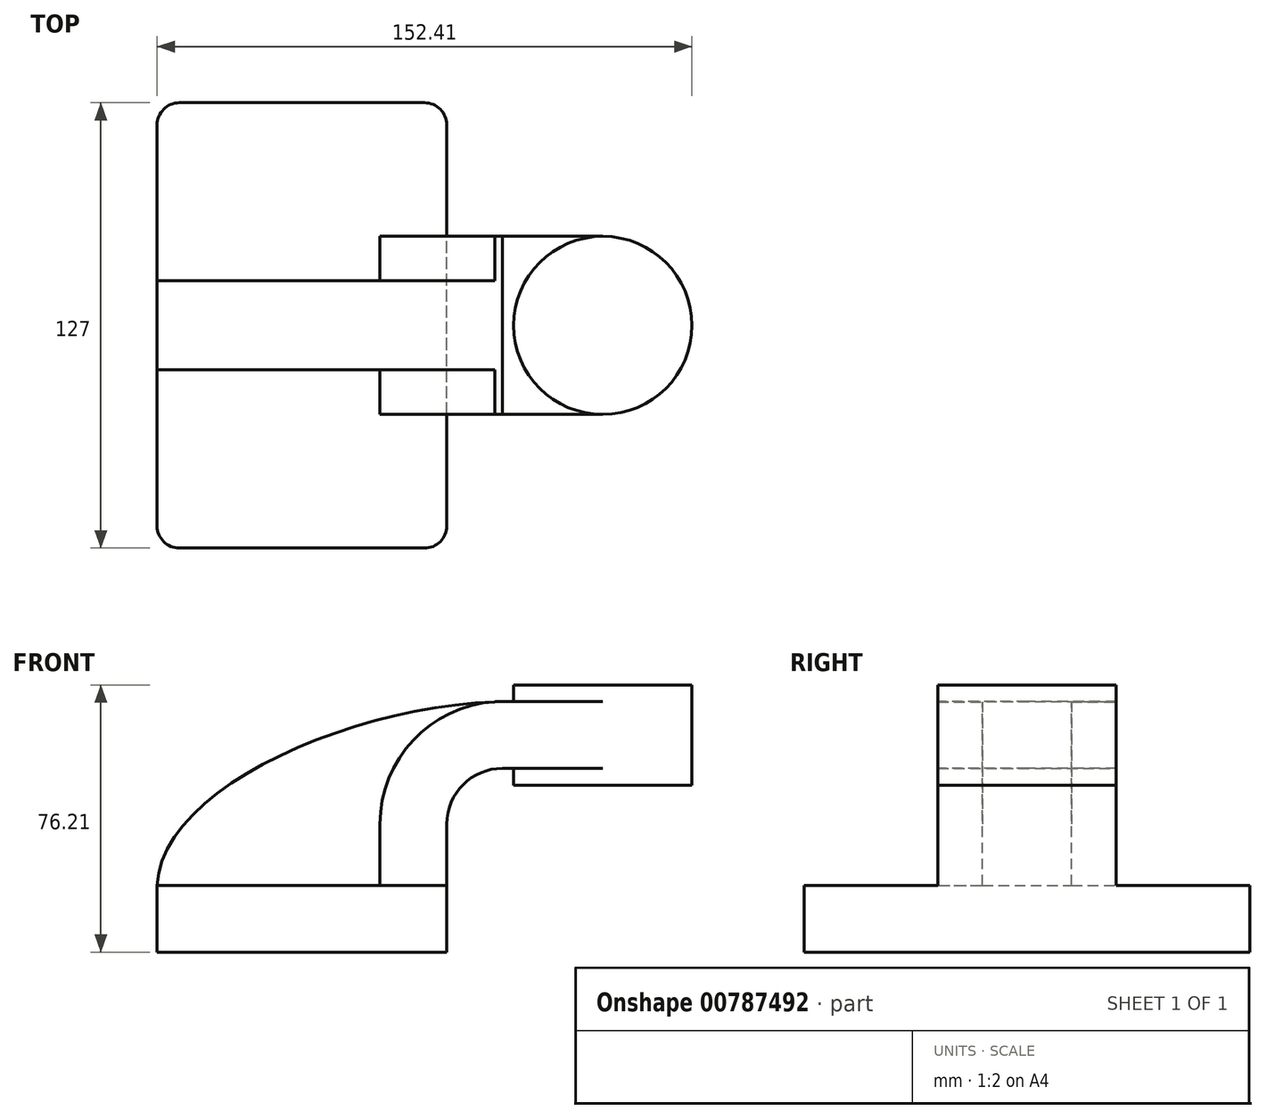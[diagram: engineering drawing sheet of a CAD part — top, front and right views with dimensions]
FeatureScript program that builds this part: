
annotation { "Feature Type Name" : "Feature", "Feature Type Description" : "" }
export const myFeature = defineFeature(function(context is Context, id is Id, definition is map)
    precondition{}
    {
        {
            var Q0;
            Q0=qCreatedBy(makeId("Front.planeOp"),FACE);
            var sketch = newSketch(context, id + "F0", { "sketchPlane" : qUnion([Q0])});
            skLineSegment(sketch, "E0.bottom", {"start": v(41.28, 9.53) * mm, "end": v(-41.27, 9.52) * mm});
            skLineSegment(sketch, "E0.top", {"start": v(41.28, -9.52) * mm, "end": v(-41.27, -9.53) * mm});
            skLineSegment(sketch, "E0.left", {"start": v(41.28, 9.53) * mm, "end": v(41.28, -9.52) * mm});
            skLineSegment(sketch, "E0.right", {"start": v(-41.27, 9.52) * mm, "end": v(-41.27, -9.53) * mm});
            skPoint(sketch, "E0.middle", {"position": v(0, 0) * mm});
            skLineSegment(sketch, "E1", {"start": v(41.27, 9.53) * mm, "end": v(41.27, 27) * mm});
            skArc(sketch, "E2", {"start": v(41.27, 27) * mm, "mid": v(45.92, 38.23) * mm, "end": v(57.15, 42.88) * mm});
            skLineSegment(sketch, "E3", {"start": v(57.15, 42.88) * mm, "end": v(85.73, 42.88) * mm});
            skLineSegment(sketch, "E4.bottom", {"start": v(60.33, 38.1) * mm, "end": v(111.13, 38.1) * mm});
            skLineSegment(sketch, "E4.top", {"start": v(60.33, 66.68) * mm, "end": v(111.13, 66.68) * mm});
            skLineSegment(sketch, "E4.left", {"start": v(60.33, 38.1) * mm, "end": v(60.32, 66.68) * mm});
            skLineSegment(sketch, "E4.right", {"start": v(111.13, 38.1) * mm, "end": v(111.13, 66.68) * mm});
            skPoint(sketch, "E4.middle", {"position": v(85.73, 52.39) * mm});
            skPoint(sketch, "E5", {"position": v(85.73, 38.1) * mm});
            skLineSegment(sketch, "E6.0", {"start": v(57.15, 61.93) * mm, "end": v(85.73, 61.93) * mm});
            skArc(sketch, "E6.1", {"start": v(22.23, 27) * mm, "mid": v(32.45, 51.7) * mm, "end": v(57.15, 61.93) * mm});
            skLineSegment(sketch, "E6.2", {"start": v(22.22, 9.52) * mm, "end": v(22.22, 27) * mm});
            skLineSegment(sketch, "E7", {"start": v(85.73, 42.88) * mm, "end": v(85.73, 61.93) * mm});
            skFitSpline(sketch, "E8", {"points": [v(-41.28, 9.52) * mm, v(57.15, 61.93) * mm], "startDerivative": vector(2.93, 82.93) * mm, "endDerivative": vector(128.83, 2.9) * mm});
            skLineSegment(sketch, "E9", {"start": v(85.73, 38.1) * mm, "end": v(85.73, 66.68) * mm});
            skSolve(sketch);
        }
        {
            var Q0;
            Q0=makeQuery(id+"F0.imprint","IMPRINT",FACE,{"disambiguationData":[TD([[makeQuery(id+"F0.imprint","IMPRINT",EDGE,{"derivedFrom":sQuery(id+"F0.wireOp",EDGE,"E0.top")}),-1.0]])]});
            extrude(context, id + "F1", {"entities" : qUnion([Q0]), "endBound" : BoundingType.SYMMETRIC, "depth" : 127 * mm, "offsetDistance" : 25.4 * mm});
        }
        {
            var Q0;
            {var subQ8=sQuery(id+"F0.wireOp",EDGE,"E1");Q0=makeQuery(id+"F0.imprint","IMPRINT",FACE,{"disambiguationData":[TD([[makeQuery(id+"F0.imprint","IMPRINT",EDGE,{"derivedFrom":subQ8}),1.0]])]});}
            var Q1;
            {var subQ0=sQuery(id+"F0.wireOp",EDGE,"E7");Q1=makeQuery(id+"F0.imprint","IMPRINT",FACE,{"disambiguationData":[TD([[makeQuery(id+"F0.imprint","IMPRINT",EDGE,{"derivedFrom":subQ0}),1.0]])]});}
            var Q2;
            {var subQ0=sQuery(id+"F0.wireOp",EDGE,"E9");var subQ1=sQuery(id+"F0.wireOp",EDGE,"E3");var subQ2=makeQuery(id+"F0.imprint","INTERSECT",VERTEX,{"derivedFrom":[subQ1,subQ0]});Q2=makeQuery(id+"F0.imprint","IMPRINT",FACE,{"disambiguationData":[TD([[makeQuery(id+"F0.imprint","IMPRINT",EDGE,{"disambiguationData":[TD([[subQ2,1.0]])],"derivedFrom":subQ1}),1.0]])]});}
            extrude(context, id + "F2", {"entities" : qUnion([Q0, Q1, Q2]), "operationType" : NewBodyOperationType.ADD, "endBound" : BoundingType.SYMMETRIC, "depth" : 50.8 * mm, "offsetDistance" : 25.4 * mm});
        }
        {
            var Q0;
            {var subQ3=sQuery(id+"F0.wireOp",EDGE,"E6.2");Q0=makeQuery(id+"F0.imprint","IMPRINT",FACE,{"disambiguationData":[TD([[makeQuery(id+"F0.imprint","IMPRINT",EDGE,{"derivedFrom":subQ3}),1.0]])]});}
            extrude(context, id + "F3", {"entities" : qUnion([Q0]), "operationType" : NewBodyOperationType.ADD, "endBound" : BoundingType.SYMMETRIC, "depth" : 25.4 * mm, "offsetDistance" : 25.4 * mm});
        }
        {
            var Q0;
            {var subQ4=sQuery(id+"F0.wireOp",EDGE,"E4.right");Q0=makeQuery(id+"F0.imprint","IMPRINT",FACE,{"disambiguationData":[TD([[makeQuery(id+"F0.imprint","IMPRINT",EDGE,{"derivedFrom":subQ4}),1.0]])]});}
            var Q1;
            Q1=sQuery(id+"F0.wireOp",EDGE,"E9");
            revolve(context, id + "F4", {"operationType" : NewBodyOperationType.ADD, "surfaceOperationType" : NewSurfaceOperationType.NEW, "entities" : qUnion([Q0]), "axis" : qUnion([Q1]), "revolveType" : RevolveType.FULL});
        }
        {
            var Q0;
            Q0=makeQuery(id+"F1.opExtrude","CAP_EDGE",EDGE,{"disambiguationData":[OSD([sQuery(id+"F0.wireOp",EDGE,"E0.left")])],"isStart":false});
            var Q1;
            Q1=makeQuery(id+"F1.opExtrude","CAP_EDGE",EDGE,{"disambiguationData":[OSD([sQuery(id+"F0.wireOp",EDGE,"E0.right")])],"isStart":false});
            var Q2;
            Q2=makeQuery(id+"F1.opExtrude","CAP_EDGE",EDGE,{"disambiguationData":[OSD([sQuery(id+"F0.wireOp",EDGE,"E0.right")])],"isStart":true});
            var Q3;
            Q3=makeQuery(id+"F1.opExtrude","CAP_EDGE",EDGE,{"disambiguationData":[OSD([sQuery(id+"F0.wireOp",EDGE,"E0.left")])],"isStart":true});
            fillet(context, id + "F5", {"entities" : qUnion([Q0, Q1, Q2, Q3]), "radius" : 6.35 * mm, "tangentPropagation" : true, "allowEdgeOverflow" : false});
        }
    });
